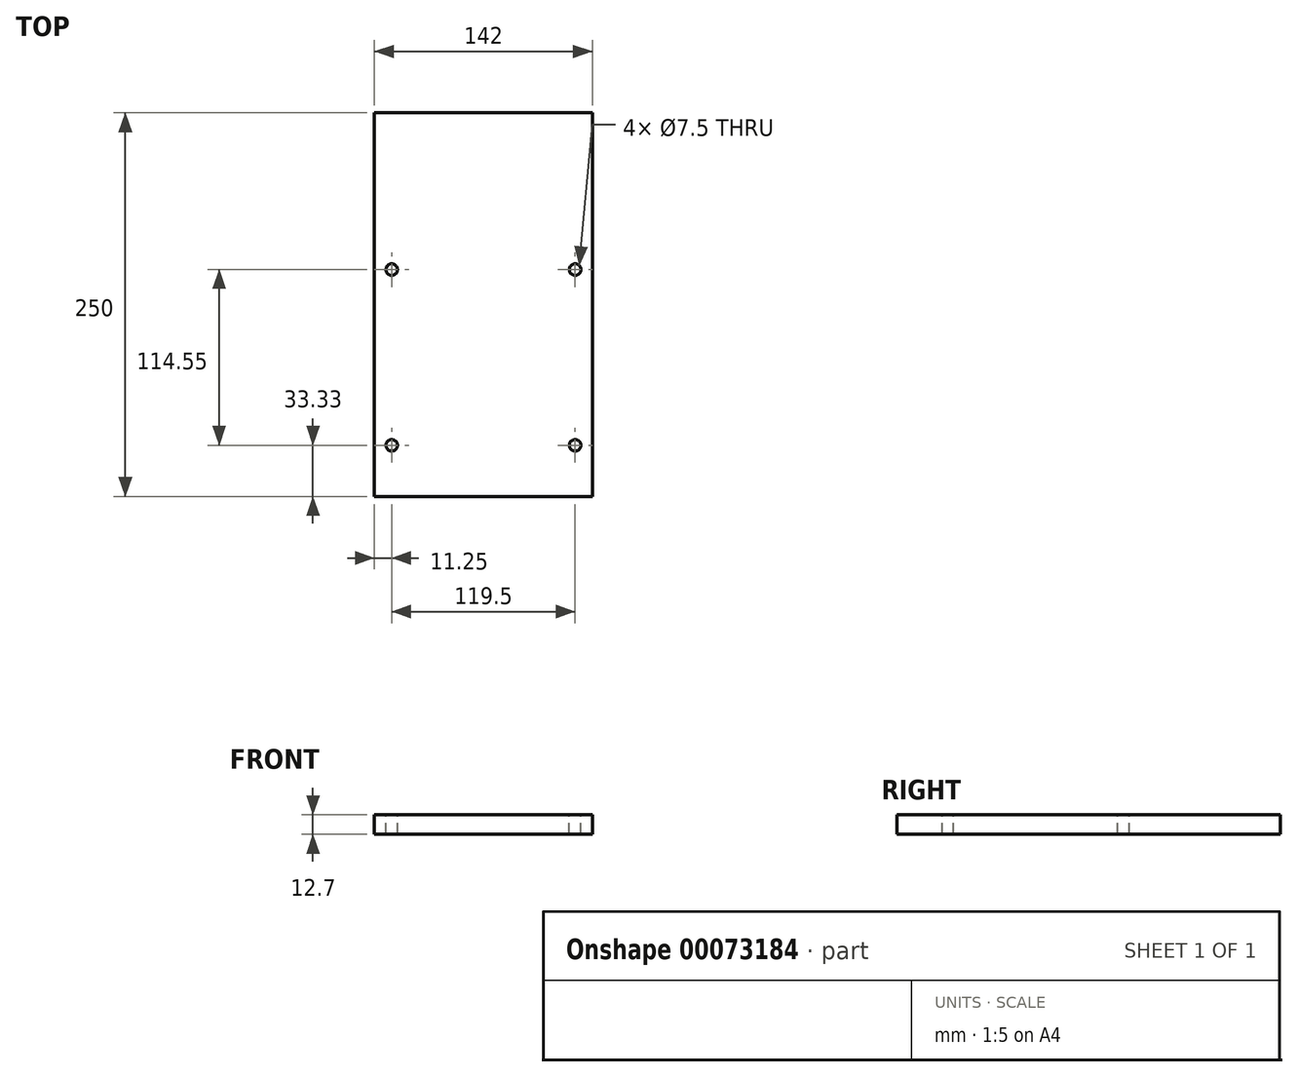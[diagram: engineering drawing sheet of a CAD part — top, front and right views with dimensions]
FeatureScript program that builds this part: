
annotation { "Feature Type Name" : "Feature", "Feature Type Description" : "" }
export const myFeature = defineFeature(function(context is Context, id is Id, definition is map)
    precondition{}
    {
        {
            var Q0;
            Q0=qCreatedBy(makeId("Top.planeOp"),FACE);
            var sketch = newSketch(context, id + "F0", { "sketchPlane" : qUnion([Q0])});
            skLineSegment(sketch, "E0.bottom", {"start": v(-71, 125) * mm, "end": v(71, 125) * mm});
            skLineSegment(sketch, "E0.top", {"start": v(-71, -125) * mm, "end": v(71, -125) * mm});
            skLineSegment(sketch, "E0.left", {"start": v(-71, 125) * mm, "end": v(-71, -125) * mm});
            skLineSegment(sketch, "E0.right", {"start": v(71, 125) * mm, "end": v(71, -125) * mm});
            skSolve(sketch);
        }
        {
            var Q0;
            Q0 = qSketchRegion(id + "F0", true);
            extrude(context, id + "F1", {"entities" : qUnion([Q0]), "depth" : 12.7 * mm});
        }
        {
            var Q0;
            Q0=makeQuery(id+"F1.opExtrude","CAP_FACE",FACE,{"disambiguationData":[OSD([sQuery(id+"F0.wireOp",EDGE,"E0.bottom"),sQuery(id+"F0.wireOp",EDGE,"E0.top"),sQuery(id+"F0.wireOp",EDGE,"E0.left"),sQuery(id+"F0.wireOp",EDGE,"E0.right")])],"isStart":false});
            var sketch = newSketch(context, id + "F2", { "sketchPlane" : qUnion([Q0])});
            skCircle(sketch, "E1", {"center": v(-59.75, 22.88) * mm, "radius": 3.75 * mm});
            skCircle(sketch, "E2", {"center": v(59.75, 22.88) * mm, "radius": 3.75 * mm});
            skCircle(sketch, "E3", {"center": v(59.75, -91.67) * mm, "radius": 3.75 * mm});
            skCircle(sketch, "E4", {"center": v(-59.75, -91.67) * mm, "radius": 3.75 * mm});
            skSolve(sketch);
        }
        {
            var Q0;
            Q0 = qSketchRegion(id + "F2", true);
            extrude(context, id + "F3", {"entities" : qUnion([Q0]), "operationType" : NewBodyOperationType.REMOVE, "endBound" : BoundingType.THROUGH_ALL, "oppositeDirection" : true, "depth" : 25 * mm});
        }
    });
